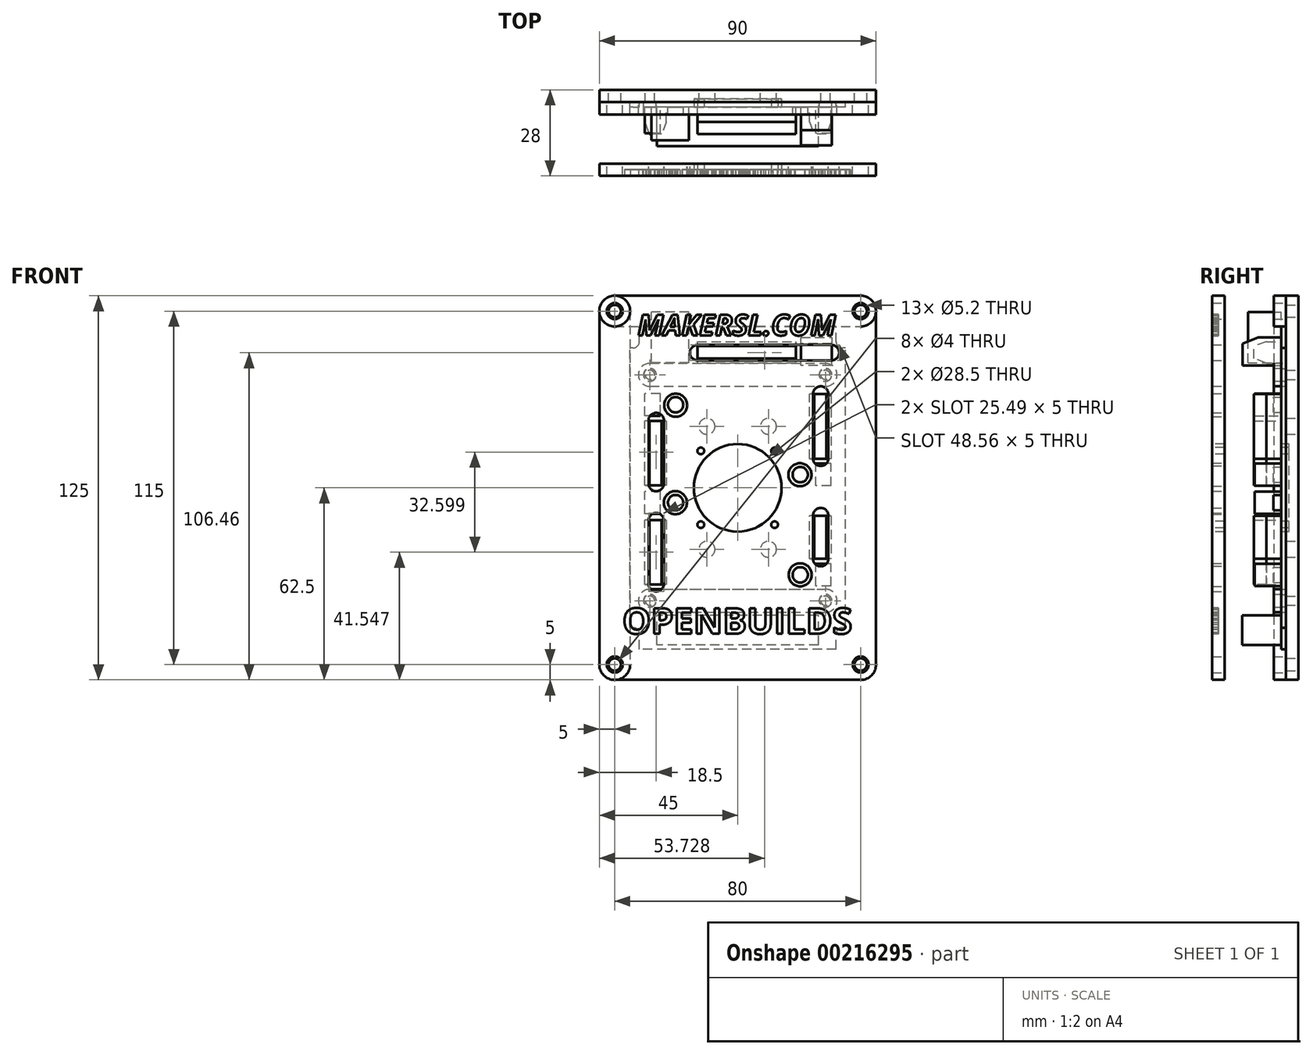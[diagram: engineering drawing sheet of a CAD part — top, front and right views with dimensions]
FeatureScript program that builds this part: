
annotation { "Feature Type Name" : "Feature", "Feature Type Description" : "" }
export const myFeature = defineFeature(function(context is Context, id is Id, definition is map)
    precondition{}
    {
        {
            var Q0;
            Q0=qCreatedBy(makeId("Front.planeOp"),FACE);
            var sketch = newSketch(context, id + "F0", { "sketchPlane" : qUnion([Q0])});
            skPoint(sketch, "E0.middle", {"position": v(0, 0) * mm});
            skLineSegment(sketch, "E1.bottom", {"start": v(10, -20) * mm, "end": v(-10, -20) * mm, "construction": true});
            skLineSegment(sketch, "E1.top", {"start": v(10, 20) * mm, "end": v(-10, 20) * mm, "construction": true});
            skLineSegment(sketch, "E1.left", {"start": v(10, -20) * mm, "end": v(10, 20) * mm, "construction": true});
            skLineSegment(sketch, "E1.right", {"start": v(-10, -20) * mm, "end": v(-10, 20) * mm, "construction": true});
            skCircle(sketch, "E2", {"center": v(-10, 20) * mm, "radius": 2.6 * mm});
            skCircle(sketch, "E3", {"center": v(10, 20) * mm, "radius": 2.6 * mm});
            skCircle(sketch, "E4", {"center": v(10, -20) * mm, "radius": 2.6 * mm});
            skCircle(sketch, "E5", {"center": v(-10, -20) * mm, "radius": 2.6 * mm});
            skLineSegment(sketch, "E6.bottom", {"start": v(28.55, -36.75) * mm, "end": v(-28.55, -36.75) * mm, "construction": true});
            skLineSegment(sketch, "E6.top", {"start": v(28.55, 36.75) * mm, "end": v(-28.55, 36.75) * mm, "construction": true});
            skLineSegment(sketch, "E6.left", {"start": v(28.55, -36.75) * mm, "end": v(28.55, 36.75) * mm, "construction": true});
            skLineSegment(sketch, "E6.right", {"start": v(-28.55, -36.75) * mm, "end": v(-28.55, 36.75) * mm, "construction": true});
            skCircle(sketch, "E7", {"center": v(-28.55, 36.75) * mm, "radius": 1.5 * mm});
            skCircle(sketch, "E8", {"center": v(28.55, 36.75) * mm, "radius": 1.5 * mm});
            skCircle(sketch, "E9", {"center": v(28.55, -36.75) * mm, "radius": 1.5 * mm});
            skCircle(sketch, "E10", {"center": v(-28.55, -36.75) * mm, "radius": 1.5 * mm});
            skLineSegment(sketch, "E11.bottom", {"start": v(40, -62.5) * mm, "end": v(-40, -62.5) * mm});
            skLineSegment(sketch, "E11.top", {"start": v(40, 62.5) * mm, "end": v(-40, 62.5) * mm});
            skLineSegment(sketch, "E11.left", {"start": v(45, -57.5) * mm, "end": v(45, 57.5) * mm});
            skLineSegment(sketch, "E11.right", {"start": v(-45, -57.5) * mm, "end": v(-45, 57.5) * mm});
            skPoint(sketch, "E12.visualSharp", {"position": v(-45, 62.5) * mm});
            skArc(sketch, "E12.filletArc", {"start": v(-40, 62.5) * mm, "mid": v(-43.54, 61.04) * mm, "end": v(-45, 57.5) * mm});
            skPoint(sketch, "E13.visualSharp", {"position": v(45, 62.5) * mm});
            skArc(sketch, "E13.filletArc", {"start": v(45, 57.5) * mm, "mid": v(43.54, 61.04) * mm, "end": v(40, 62.5) * mm});
            skPoint(sketch, "E14.visualSharp", {"position": v(45, -62.5) * mm});
            skArc(sketch, "E14.filletArc", {"start": v(40, -62.5) * mm, "mid": v(43.54, -61.04) * mm, "end": v(45, -57.5) * mm});
            skPoint(sketch, "E15.visualSharp", {"position": v(-45, -62.5) * mm});
            skArc(sketch, "E15.filletArc", {"start": v(-45, -57.5) * mm, "mid": v(-43.54, -61.04) * mm, "end": v(-40, -62.5) * mm});
            skCircle(sketch, "E16", {"center": v(-40, 57.5) * mm, "radius": 2 * mm});
            skCircle(sketch, "E17", {"center": v(40, 57.5) * mm, "radius": 2 * mm});
            skCircle(sketch, "E18", {"center": v(-40, -57.5) * mm, "radius": 2 * mm});
            skCircle(sketch, "E19", {"center": v(40, -57.5) * mm, "radius": 2 * mm});
            skSolve(sketch);
        }
        {
            var Q0;
            Q0=qSketchRegion(id+"F0",true);
            extrude(context, id + "F1", {"entities" : qUnion([Q0]), "depth" : 4 * mm});
        }
        {
            var Q0;
            Q0=makeQuery(id+"F1.opExtrude","CAP_FACE",FACE,{"disambiguationData":[OSD([sQuery(id+"F0.wireOp",EDGE,"E2"),sQuery(id+"F0.wireOp",EDGE,"E3"),sQuery(id+"F0.wireOp",EDGE,"E4"),sQuery(id+"F0.wireOp",EDGE,"E5"),sQuery(id+"F0.wireOp",EDGE,"E7"),sQuery(id+"F0.wireOp",EDGE,"E8"),sQuery(id+"F0.wireOp",EDGE,"E9"),sQuery(id+"F0.wireOp",EDGE,"E10"),sQuery(id+"F0.wireOp",EDGE,"E11.bottom"),sQuery(id+"F0.wireOp",EDGE,"E11.top"),sQuery(id+"F0.wireOp",EDGE,"E11.left"),sQuery(id+"F0.wireOp",EDGE,"E11.right"),sQuery(id+"F0.wireOp",EDGE,"E12.filletArc"),sQuery(id+"F0.wireOp",EDGE,"E13.filletArc"),sQuery(id+"F0.wireOp",EDGE,"E14.filletArc"),sQuery(id+"F0.wireOp",EDGE,"E15.filletArc"),sQuery(id+"F0.wireOp",EDGE,"E16"),sQuery(id+"F0.wireOp",EDGE,"E17"),sQuery(id+"F0.wireOp",EDGE,"E18"),sQuery(id+"F0.wireOp",EDGE,"E19")])],"isStart":false});
            var sketch = newSketch(context, id + "F2", { "sketchPlane" : qUnion([Q0])});
            skCircle(sketch, "E20", {"center": v(-28.55, 36.75) * mm, "radius": 2.1 * mm});
            skCircle(sketch, "E21", {"center": v(28.55, 36.75) * mm, "radius": 2.1 * mm});
            skCircle(sketch, "E22", {"center": v(-28.55, -36.75) * mm, "radius": 2.1 * mm});
            skCircle(sketch, "E23", {"center": v(28.55, -36.75) * mm, "radius": 2.1 * mm});
            skLineSegment(sketch, "E24", {"start": v(-28.55, -36.75) * mm, "end": v(28.55, -36.75) * mm});
            skLineSegment(sketch, "E25", {"start": v(-28.55, 36.75) * mm, "end": v(28.55, 36.75) * mm});
            skArc(sketch, "E26.0.startCap", {"start": v(-28.55, 33) * mm, "mid": v(-32.3, 36.75) * mm, "end": v(-28.55, 40.5) * mm});
            skArc(sketch, "E26.0.endCap", {"start": v(28.55, 40.5) * mm, "mid": v(32.3, 36.75) * mm, "end": v(28.55, 33) * mm});
            skLineSegment(sketch, "E26.0.left", {"start": v(-28.55, 40.5) * mm, "end": v(28.55, 40.5) * mm});
            skLineSegment(sketch, "E26.0.right", {"start": v(-28.55, 33) * mm, "end": v(28.55, 33) * mm});
            skArc(sketch, "E27.0.startCap", {"start": v(-28.55, -40.5) * mm, "mid": v(-32.3, -36.75) * mm, "end": v(-28.55, -33) * mm});
            skArc(sketch, "E27.0.endCap", {"start": v(28.55, -33) * mm, "mid": v(32.3, -36.75) * mm, "end": v(28.55, -40.5) * mm});
            skLineSegment(sketch, "E27.0.left", {"start": v(-28.55, -33) * mm, "end": v(28.55, -33) * mm});
            skLineSegment(sketch, "E27.0.right", {"start": v(-28.55, -40.5) * mm, "end": v(28.55, -40.5) * mm});
            skSolve(sketch);
        }
        {
            var Q0;
            Q0=makeQuery(id+"F2.imprint","IMPRINT",FACE,{"disambiguationData":[TD([[makeQuery(id+"F2.imprint","IMPRINT",EDGE,{"derivedFrom":sQuery(id+"F2.wireOp",EDGE,"E20")}),-1.0]])]});
            var Q1;
            Q1=makeQuery(id+"F2.imprint","IMPRINT",FACE,{"disambiguationData":[TD([[makeQuery(id+"F2.imprint","IMPRINT",EDGE,{"derivedFrom":sQuery(id+"F2.wireOp",EDGE,"E22")}),-1.0]])]});
            extrude(context, id + "F3", {"entities" : qUnion([Q0, Q1]), "depth" : 4 * mm});
        }
        {
            var Q0;
            Q0=makeQuery(id+"F1.opExtrude","CAP_FACE",FACE,{"disambiguationData":[OSD([sQuery(id+"F0.wireOp",EDGE,"E2"),sQuery(id+"F0.wireOp",EDGE,"E3"),sQuery(id+"F0.wireOp",EDGE,"E4"),sQuery(id+"F0.wireOp",EDGE,"E5"),sQuery(id+"F0.wireOp",EDGE,"E7"),sQuery(id+"F0.wireOp",EDGE,"E8"),sQuery(id+"F0.wireOp",EDGE,"E9"),sQuery(id+"F0.wireOp",EDGE,"E10"),sQuery(id+"F0.wireOp",EDGE,"E11.bottom"),sQuery(id+"F0.wireOp",EDGE,"E11.top"),sQuery(id+"F0.wireOp",EDGE,"E11.left"),sQuery(id+"F0.wireOp",EDGE,"E11.right"),sQuery(id+"F0.wireOp",EDGE,"E12.filletArc"),sQuery(id+"F0.wireOp",EDGE,"E13.filletArc"),sQuery(id+"F0.wireOp",EDGE,"E14.filletArc"),sQuery(id+"F0.wireOp",EDGE,"E15.filletArc"),sQuery(id+"F0.wireOp",EDGE,"E16"),sQuery(id+"F0.wireOp",EDGE,"E17"),sQuery(id+"F0.wireOp",EDGE,"E18"),sQuery(id+"F0.wireOp",EDGE,"E19")])],"isStart":false});
            var sketch = newSketch(context, id + "F4", { "sketchPlane" : qUnion([Q0])});
            skCircle(sketch, "E28", {"center": v(-40, 57.5) * mm, "radius": 2.6 * mm});
            skCircle(sketch, "E29", {"center": v(40, 57.5) * mm, "radius": 2.6 * mm});
            skLineSegment(sketch, "E30", {"start": v(-40, 57.5) * mm, "end": v(40, 57.5) * mm});
            skArc(sketch, "E31.0.startCap", {"start": v(-40, 52.5) * mm, "mid": v(-45, 57.5) * mm, "end": v(-40, 62.5) * mm});
            skArc(sketch, "E31.0.endCap", {"start": v(40, 62.5) * mm, "mid": v(45, 57.5) * mm, "end": v(40, 52.5) * mm});
            skLineSegment(sketch, "E31.0.left", {"start": v(-40, 62.5) * mm, "end": v(40, 62.5) * mm});
            skLineSegment(sketch, "E31.0.right", {"start": v(-40, 52.5) * mm, "end": v(40, 52.5) * mm});
            skSolve(sketch);
        }
        {
            var Q0;
            Q0=makeQuery(id+"F4.imprint","IMPRINT",FACE,{"disambiguationData":[TD([[makeQuery(id+"F4.imprint","IMPRINT",EDGE,{"derivedFrom":sQuery(id+"F4.wireOp",EDGE,"E28")}),-1.0]])]});
            extrude(context, id + "F5", {"entities" : qUnion([Q0]), "depth" : 4 * mm});
        }
        {
            var Q0;
            Q0=makeQuery(id+"F1.opExtrude","CAP_FACE",FACE,{"disambiguationData":[OSD([sQuery(id+"F0.wireOp",EDGE,"E2"),sQuery(id+"F0.wireOp",EDGE,"E3"),sQuery(id+"F0.wireOp",EDGE,"E4"),sQuery(id+"F0.wireOp",EDGE,"E5"),sQuery(id+"F0.wireOp",EDGE,"E7"),sQuery(id+"F0.wireOp",EDGE,"E8"),sQuery(id+"F0.wireOp",EDGE,"E9"),sQuery(id+"F0.wireOp",EDGE,"E10"),sQuery(id+"F0.wireOp",EDGE,"E11.bottom"),sQuery(id+"F0.wireOp",EDGE,"E11.top"),sQuery(id+"F0.wireOp",EDGE,"E11.left"),sQuery(id+"F0.wireOp",EDGE,"E11.right"),sQuery(id+"F0.wireOp",EDGE,"E12.filletArc"),sQuery(id+"F0.wireOp",EDGE,"E13.filletArc"),sQuery(id+"F0.wireOp",EDGE,"E14.filletArc"),sQuery(id+"F0.wireOp",EDGE,"E15.filletArc"),sQuery(id+"F0.wireOp",EDGE,"E16"),sQuery(id+"F0.wireOp",EDGE,"E17"),sQuery(id+"F0.wireOp",EDGE,"E18"),sQuery(id+"F0.wireOp",EDGE,"E19")])],"isStart":false});
            var sketch = newSketch(context, id + "F6", { "sketchPlane" : qUnion([Q0])});
            skCircle(sketch, "E32", {"center": v(-40, -57.5) * mm, "radius": 2.6 * mm});
            skCircle(sketch, "E33", {"center": v(-40, 57.5) * mm, "radius": 2.6 * mm});
            skLineSegment(sketch, "E34", {"start": v(-40, 57.5) * mm, "end": v(-40, -57.5) * mm});
            skArc(sketch, "E35.0.startCap", {"start": v(-45, 57.5) * mm, "mid": v(-40, 62.5) * mm, "end": v(-35, 57.5) * mm});
            skArc(sketch, "E35.0.endCap", {"start": v(-35, -57.5) * mm, "mid": v(-40, -62.5) * mm, "end": v(-45, -57.5) * mm});
            skLineSegment(sketch, "E35.0.left", {"start": v(-35, 57.5) * mm, "end": v(-35, -57.5) * mm});
            skLineSegment(sketch, "E35.0.right", {"start": v(-45, 57.5) * mm, "end": v(-45, -57.5) * mm});
            skSolve(sketch);
        }
        {
            var Q0;
            Q0=makeQuery(id+"F6.imprint","IMPRINT",FACE,{"disambiguationData":[TD([[makeQuery(id+"F6.imprint","IMPRINT",EDGE,{"derivedFrom":sQuery(id+"F6.wireOp",EDGE,"E32")}),-1.0]])]});
            extrude(context, id + "F7", {"entities" : qUnion([Q0]), "depth" : 4 * mm});
        }
        {
            var Q0;
            Q0=makeQuery(id+"F1.opExtrude","CAP_FACE",FACE,{"disambiguationData":[OSD([sQuery(id+"F0.wireOp",EDGE,"E2"),sQuery(id+"F0.wireOp",EDGE,"E3"),sQuery(id+"F0.wireOp",EDGE,"E4"),sQuery(id+"F0.wireOp",EDGE,"E5"),sQuery(id+"F0.wireOp",EDGE,"E7"),sQuery(id+"F0.wireOp",EDGE,"E8"),sQuery(id+"F0.wireOp",EDGE,"E9"),sQuery(id+"F0.wireOp",EDGE,"E10"),sQuery(id+"F0.wireOp",EDGE,"E11.bottom"),sQuery(id+"F0.wireOp",EDGE,"E11.top"),sQuery(id+"F0.wireOp",EDGE,"E11.left"),sQuery(id+"F0.wireOp",EDGE,"E11.right"),sQuery(id+"F0.wireOp",EDGE,"E12.filletArc"),sQuery(id+"F0.wireOp",EDGE,"E13.filletArc"),sQuery(id+"F0.wireOp",EDGE,"E14.filletArc"),sQuery(id+"F0.wireOp",EDGE,"E15.filletArc"),sQuery(id+"F0.wireOp",EDGE,"E16"),sQuery(id+"F0.wireOp",EDGE,"E17"),sQuery(id+"F0.wireOp",EDGE,"E18"),sQuery(id+"F0.wireOp",EDGE,"E19")])],"isStart":false});
            var sketch = newSketch(context, id + "F8", { "sketchPlane" : qUnion([Q0])});
            skLineSegment(sketch, "E36.bottom", {"start": v(32, -52.5) * mm, "end": v(-32, -52.5) * mm});
            skLineSegment(sketch, "E36.top", {"start": v(32, 52.5) * mm, "end": v(-32, 52.5) * mm});
            skLineSegment(sketch, "E36.left", {"start": v(35, -45.5) * mm, "end": v(35, 45.5) * mm});
            skLineSegment(sketch, "E36.right", {"start": v(-35, -45.5) * mm, "end": v(-35, 45.5) * mm});
            skPoint(sketch, "E36.middle", {"position": v(0, 0) * mm});
            skLineSegment(sketch, "E37.bottom", {"start": v(-34, 45.5) * mm, "end": v(-35, 45.5) * mm});
            skLineSegment(sketch, "E37.left", {"start": v(-32, 47.5) * mm, "end": v(-32, 52.5) * mm});
            skPoint(sketch, "E37.middle", {"position": v(-35, 52.5) * mm});
            skLineSegment(sketch, "E38.bottom", {"start": v(35, 45.5) * mm, "end": v(34, 45.5) * mm});
            skLineSegment(sketch, "E38.right", {"start": v(32, 47.5) * mm, "end": v(32, 52.5) * mm});
            skPoint(sketch, "E38.middle", {"position": v(35, 52.5) * mm});
            skLineSegment(sketch, "E39.top", {"start": v(35, -45.5) * mm, "end": v(34, -45.5) * mm});
            skLineSegment(sketch, "E39.right", {"start": v(32, -52.5) * mm, "end": v(32, -47.5) * mm});
            skPoint(sketch, "E39.middle", {"position": v(35, -52.5) * mm});
            skLineSegment(sketch, "E40.top", {"start": v(-35, -45.5) * mm, "end": v(-34, -45.5) * mm});
            skLineSegment(sketch, "E40.right", {"start": v(-32, -52.5) * mm, "end": v(-32, -47.5) * mm});
            skPoint(sketch, "E40.middle", {"position": v(-35, -52.5) * mm});
            skPoint(sketch, "E40.left.end.orphan", {"position": v(-38, -45.5) * mm});
            skPoint(sketch, "E40.bottom.start.orphan", {"position": v(-38, -59.5) * mm});
            skPoint(sketch, "E41.orphan", {"position": v(-32, -59.5) * mm});
            skPoint(sketch, "E42.visualSharp", {"position": v(-32, -45.5) * mm});
            skArc(sketch, "E42.filletArc", {"start": v(-32, -47.5) * mm, "mid": v(-32.59, -46.09) * mm, "end": v(-34, -45.5) * mm});
            skPoint(sketch, "E43.visualSharp", {"position": v(32, -45.5) * mm});
            skArc(sketch, "E43.filletArc", {"start": v(34, -45.5) * mm, "mid": v(32.59, -46.09) * mm, "end": v(32, -47.5) * mm});
            skPoint(sketch, "E44.visualSharp", {"position": v(32, 45.5) * mm});
            skArc(sketch, "E44.filletArc", {"start": v(32, 47.5) * mm, "mid": v(32.59, 46.09) * mm, "end": v(34, 45.5) * mm});
            skPoint(sketch, "E45.visualSharp", {"position": v(-32, 45.5) * mm});
            skArc(sketch, "E45.filletArc", {"start": v(-34, 45.5) * mm, "mid": v(-32.59, 46.09) * mm, "end": v(-32, 47.5) * mm});
            skPoint(sketch, "E37.right.end.orphan", {"position": v(-38, 59.5) * mm});
            skPoint(sketch, "E46.orphan", {"position": v(-38, 45.5) * mm});
            skPoint(sketch, "E47.orphan", {"position": v(-32, 59.5) * mm});
            skPoint(sketch, "E38.left.start.orphan", {"position": v(38, 45.5) * mm});
            skPoint(sketch, "E38.top.end.orphan", {"position": v(32, 59.5) * mm});
            skPoint(sketch, "E38.top.start.orphan", {"position": v(38, 59.5) * mm});
            skPoint(sketch, "E39.bottom.end.orphan", {"position": v(32, -59.5) * mm});
            skPoint(sketch, "E39.left.end.orphan", {"position": v(38, -45.5) * mm});
            skPoint(sketch, "E39.left.start.orphan", {"position": v(38, -59.5) * mm});
            skCircle(sketch, "E48", {"center": v(-28.55, 36.75) * mm, "radius": 2 * mm});
            skCircle(sketch, "E49", {"center": v(28.55, 36.75) * mm, "radius": 2 * mm});
            skCircle(sketch, "E50", {"center": v(28.55, -36.75) * mm, "radius": 2 * mm});
            skCircle(sketch, "E51", {"center": v(-28.55, -36.75) * mm, "radius": 2 * mm});
            skSolve(sketch);
        }
        {
            var Q0;
            Q0=qSketchRegion(id+"F8",true);
            extrude(context, id + "F9", {"entities" : qUnion([Q0]), "depth" : 1.6 * mm});
        }
        {
            var Q0;
            Q0=makeQuery(id+"F9.opExtrude","CAP_FACE",FACE,{"disambiguationData":[OSD([sQuery(id+"F8.wireOp",EDGE,"E36.bottom"),sQuery(id+"F8.wireOp",EDGE,"E36.top"),sQuery(id+"F8.wireOp",EDGE,"E36.left"),sQuery(id+"F8.wireOp",EDGE,"E36.right"),sQuery(id+"F8.wireOp",EDGE,"E37.bottom"),sQuery(id+"F8.wireOp",EDGE,"E37.left"),sQuery(id+"F8.wireOp",EDGE,"E38.bottom"),sQuery(id+"F8.wireOp",EDGE,"E38.right"),sQuery(id+"F8.wireOp",EDGE,"E39.top"),sQuery(id+"F8.wireOp",EDGE,"E39.right"),sQuery(id+"F8.wireOp",EDGE,"E40.top"),sQuery(id+"F8.wireOp",EDGE,"E40.right"),sQuery(id+"F8.wireOp",EDGE,"E42.filletArc"),sQuery(id+"F8.wireOp",EDGE,"E43.filletArc"),sQuery(id+"F8.wireOp",EDGE,"E44.filletArc"),sQuery(id+"F8.wireOp",EDGE,"E45.filletArc"),sQuery(id+"F8.wireOp",EDGE,"E48"),sQuery(id+"F8.wireOp",EDGE,"E49"),sQuery(id+"F8.wireOp",EDGE,"E50"),sQuery(id+"F8.wireOp",EDGE,"E51")])],"isStart":false});
            var sketch = newSketch(context, id + "F10", { "sketchPlane" : qUnion([Q0])});
            skLineSegment(sketch, "E52.bottom", {"start": v(-15.9, 40.7) * mm, "end": v(-28.1, 40.7) * mm});
            skLineSegment(sketch, "E52.top", {"start": v(-15.9, 57.2) * mm, "end": v(-28.1, 57.2) * mm});
            skLineSegment(sketch, "E52.left", {"start": v(-15.9, 40.7) * mm, "end": v(-15.9, 57.2) * mm});
            skLineSegment(sketch, "E52.right", {"start": v(-28.1, 40.7) * mm, "end": v(-28.1, 57.2) * mm});
            skPoint(sketch, "E52.middle", {"position": v(-22, 48.95) * mm});
            skLineSegment(sketch, "E53.bottom", {"start": v(30.6, 39.8) * mm, "end": v(20.6, 39.8) * mm});
            skLineSegment(sketch, "E53.top", {"start": v(30.6, 48.9) * mm, "end": v(20.6, 48.9) * mm});
            skLineSegment(sketch, "E53.left", {"start": v(30.6, 39.8) * mm, "end": v(30.6, 48.9) * mm});
            skLineSegment(sketch, "E53.right", {"start": v(20.6, 39.8) * mm, "end": v(20.6, 48.9) * mm});
            skPoint(sketch, "E53.middle", {"position": v(25.6, 44.35) * mm});
            skLineSegment(sketch, "E54.bottom", {"start": v(18.9, 40.6) * mm, "end": v(-13.1, 40.6) * mm});
            skLineSegment(sketch, "E54.top", {"start": v(18.9, 47.6) * mm, "end": v(-13.1, 47.6) * mm});
            skLineSegment(sketch, "E54.left", {"start": v(18.9, 40.6) * mm, "end": v(18.9, 47.6) * mm});
            skLineSegment(sketch, "E54.right", {"start": v(-13.1, 40.6) * mm, "end": v(-13.1, 47.6) * mm});
            skPoint(sketch, "E54.middle", {"position": v(2.9, 44.1) * mm});
            skLineSegment(sketch, "E55.bottom", {"start": v(30.35, 9.5) * mm, "end": v(23.35, 9.5) * mm});
            skLineSegment(sketch, "E55.top", {"start": v(30.35, 30.5) * mm, "end": v(23.35, 30.5) * mm});
            skLineSegment(sketch, "E55.left", {"start": v(30.35, 9.5) * mm, "end": v(30.35, 30.5) * mm});
            skLineSegment(sketch, "E55.right", {"start": v(23.35, 9.5) * mm, "end": v(23.35, 30.5) * mm});
            skPoint(sketch, "E55.middle", {"position": v(26.85, 20) * mm});
            skLineSegment(sketch, "E56.bottom", {"start": v(-23.2, -31.5) * mm, "end": v(-30.2, -31.5) * mm});
            skLineSegment(sketch, "E56.top", {"start": v(-23.2, -10.5) * mm, "end": v(-30.2, -10.5) * mm});
            skLineSegment(sketch, "E56.left", {"start": v(-23.2, -31.5) * mm, "end": v(-23.2, -10.5) * mm});
            skLineSegment(sketch, "E56.right", {"start": v(-30.2, -31.5) * mm, "end": v(-30.2, -10.5) * mm});
            skPoint(sketch, "E56.middle", {"position": v(-26.7, -21) * mm});
            skLineSegment(sketch, "E57.bottom", {"start": v(-23.2, 0.8) * mm, "end": v(-30.2, 0.8) * mm});
            skLineSegment(sketch, "E57.top", {"start": v(-23.2, 21.8) * mm, "end": v(-30.2, 21.8) * mm});
            skLineSegment(sketch, "E57.left", {"start": v(-23.2, 0.8) * mm, "end": v(-23.2, 21.8) * mm});
            skLineSegment(sketch, "E57.right", {"start": v(-30.2, 0.8) * mm, "end": v(-30.2, 21.8) * mm});
            skPoint(sketch, "E57.middle", {"position": v(-26.7, 11.3) * mm});
            skLineSegment(sketch, "E58.bottom", {"start": v(26.25, -51.1) * mm, "end": v(-26.25, -51.1) * mm});
            skLineSegment(sketch, "E58.top", {"start": v(26.25, -41.5) * mm, "end": v(-26.25, -41.5) * mm});
            skLineSegment(sketch, "E58.left", {"start": v(26.25, -51.1) * mm, "end": v(26.25, -41.5) * mm});
            skLineSegment(sketch, "E58.right", {"start": v(-26.25, -51.1) * mm, "end": v(-26.25, -41.5) * mm});
            skPoint(sketch, "E58.middle", {"position": v(0, -46.3) * mm});
            skLineSegment(sketch, "E59.bottom", {"start": v(30.35, -23.1) * mm, "end": v(23.35, -23.1) * mm});
            skLineSegment(sketch, "E59.top", {"start": v(30.35, -9.1) * mm, "end": v(23.35, -9.1) * mm});
            skLineSegment(sketch, "E59.left", {"start": v(30.35, -23.1) * mm, "end": v(30.35, -9.1) * mm});
            skLineSegment(sketch, "E59.right", {"start": v(23.35, -23.1) * mm, "end": v(23.35, -9.1) * mm});
            skPoint(sketch, "E59.middle", {"position": v(26.85, -16.1) * mm});
            skLineSegment(sketch, "E60.bottom", {"start": v(30.35, -31.95) * mm, "end": v(25.35, -31.95) * mm});
            skLineSegment(sketch, "E60.top", {"start": v(30.35, -24.7) * mm, "end": v(25.35, -24.7) * mm});
            skLineSegment(sketch, "E60.left", {"start": v(30.35, -31.95) * mm, "end": v(30.35, -24.7) * mm});
            skLineSegment(sketch, "E60.right", {"start": v(25.35, -31.95) * mm, "end": v(25.35, -24.7) * mm});
            skPoint(sketch, "E60.middle", {"position": v(27.85, -28.33) * mm});
            skLineSegment(sketch, "E61.bottom", {"start": v(30.35, 0.65) * mm, "end": v(25.35, 0.65) * mm});
            skLineSegment(sketch, "E61.top", {"start": v(30.35, 7.9) * mm, "end": v(25.35, 7.9) * mm});
            skLineSegment(sketch, "E61.left", {"start": v(30.35, 0.65) * mm, "end": v(30.35, 7.9) * mm});
            skLineSegment(sketch, "E61.right", {"start": v(25.35, 0.65) * mm, "end": v(25.35, 7.9) * mm});
            skPoint(sketch, "E61.middle", {"position": v(27.85, 4.28) * mm});
            skLineSegment(sketch, "E62.bottom", {"start": v(-25.2, 23.4) * mm, "end": v(-30.2, 23.4) * mm});
            skLineSegment(sketch, "E62.top", {"start": v(-25.2, 30.65) * mm, "end": v(-30.2, 30.65) * mm});
            skLineSegment(sketch, "E62.left", {"start": v(-25.2, 23.4) * mm, "end": v(-25.2, 30.65) * mm});
            skLineSegment(sketch, "E62.right", {"start": v(-30.2, 23.4) * mm, "end": v(-30.2, 30.65) * mm});
            skPoint(sketch, "E62.middle", {"position": v(-27.7, 27.02) * mm});
            skLineSegment(sketch, "E63.bottom", {"start": v(-25.2, -8.45) * mm, "end": v(-30.2, -8.45) * mm});
            skLineSegment(sketch, "E63.top", {"start": v(-25.2, -1.2) * mm, "end": v(-30.2, -1.2) * mm});
            skLineSegment(sketch, "E63.left", {"start": v(-25.2, -8.45) * mm, "end": v(-25.2, -1.2) * mm});
            skLineSegment(sketch, "E63.right", {"start": v(-30.2, -8.45) * mm, "end": v(-30.2, -1.2) * mm});
            skPoint(sketch, "E63.middle", {"position": v(-27.7, -4.83) * mm});
            skCircle(sketch, "E64", {"center": v(-20.2, 27.02) * mm, "radius": 2.5 * mm});
            skCircle(sketch, "E65", {"center": v(20.35, 4.28) * mm, "radius": 2.5 * mm});
            skCircle(sketch, "E66", {"center": v(20.35, -28.33) * mm, "radius": 2.5 * mm});
            skCircle(sketch, "E67", {"center": v(-20.2, -4.83) * mm, "radius": 2.5 * mm});
            skPoint(sketch, "E67.centerSnap0", {"position": v(-25.2, -4.83) * mm});
            skSolve(sketch);
        }
        {
            var Q0;
            {var subQ0=sQuery(id+"F10.wireOp",EDGE,"E52.top");Q0=makeQuery(id+"F10.imprint","IMPRINT",FACE,{"disambiguationData":[TD([[makeQuery(id+"F10.imprint","IMPRINT",EDGE,{"derivedFrom":subQ0}),1.0]])]});}
            var Q1;
            {var subQ0=sQuery(id+"F10.wireOp",EDGE,"E52.bottom");Q1=makeQuery(id+"F10.imprint","IMPRINT",FACE,{"disambiguationData":[TD([[makeQuery(id+"F10.imprint","IMPRINT",EDGE,{"derivedFrom":subQ0}),-1.0]])]});}
            extrude(context, id + "F11", {"entities" : qUnion([Q0, Q1]), "depth" : 10.8 * mm});
        }
        {
            var Q0;
            Q0=makeQuery(id+"F10.imprint","IMPRINT",FACE,{"disambiguationData":[TD([[makeQuery(id+"F10.imprint","IMPRINT",EDGE,{"derivedFrom":sQuery(id+"F10.wireOp",EDGE,"E53.bottom")}),-1.0]])]});
            extrude(context, id + "F12", {"entities" : qUnion([Q0]), "depth" : 12.5 * mm});
        }
        {
            var Q0;
            Q0=makeQuery(id+"F10.imprint","IMPRINT",FACE,{"disambiguationData":[TD([[makeQuery(id+"F10.imprint","IMPRINT",EDGE,{"derivedFrom":sQuery(id+"F10.wireOp",EDGE,"E54.bottom")}),-1.0]])]});
            extrude(context, id + "F13", {"entities" : qUnion([Q0]), "depth" : 8.85 * mm});
        }
        {
            var Q0;
            Q0=makeQuery(id+"F13.opExtrude","CAP_EDGE",EDGE,{"disambiguationData":[OSD([sQuery(id+"F10.wireOp",EDGE,"E54.top")])],"isStart":false});
            var Q1;
            Q1=makeQuery(id+"F13.opExtrude","CAP_EDGE",EDGE,{"disambiguationData":[OSD([sQuery(id+"F10.wireOp",EDGE,"E54.bottom")])],"isStart":false});
            chamfer(context, id + "F14", {"entities" : qUnion([Q0, Q1]), "chamferType" : ChamferType.TWO_OFFSETS, "width1" : 1.5 * mm, "oppositeDirection" : false, "width2" : 4 * mm, "tangentPropagation" : true});
        }
        {
            var Q0;
            Q0=makeQuery(id+"F12.opExtrude","CAP_EDGE",EDGE,{"disambiguationData":[OSD([sQuery(id+"F10.wireOp",EDGE,"E53.top")])],"isStart":false});
            chamfer(context, id + "F15", {"entities" : qUnion([Q0]), "chamferType" : ChamferType.TWO_OFFSETS, "width1" : 2 * mm, "oppositeDirection" : false, "width2" : 5 * mm, "tangentPropagation" : true});
        }
        {
            var Q0;
            Q0=makeQuery(id+"F10.imprint","IMPRINT",FACE,{"disambiguationData":[TD([[makeQuery(id+"F10.imprint","IMPRINT",EDGE,{"derivedFrom":sQuery(id+"F10.wireOp",EDGE,"E55.bottom")}),-1.0]])]});
            var Q1;
            Q1=makeQuery(id+"F10.imprint","IMPRINT",FACE,{"disambiguationData":[TD([[makeQuery(id+"F10.imprint","IMPRINT",EDGE,{"derivedFrom":sQuery(id+"F10.wireOp",EDGE,"E57.bottom")}),-1.0]])]});
            var Q2;
            Q2=makeQuery(id+"F10.imprint","IMPRINT",FACE,{"disambiguationData":[TD([[makeQuery(id+"F10.imprint","IMPRINT",EDGE,{"derivedFrom":sQuery(id+"F10.wireOp",EDGE,"E56.bottom")}),-1.0]])]});
            extrude(context, id + "F16", {"entities" : qUnion([Q0, Q1, Q2]), "depth" : 8.8 * mm});
        }
        {
            var Q0;
            Q0=makeQuery(id+"F10.imprint","IMPRINT",FACE,{"disambiguationData":[TD([[makeQuery(id+"F10.imprint","IMPRINT",EDGE,{"derivedFrom":sQuery(id+"F10.wireOp",EDGE,"E58.bottom")}),-1.0]])]});
            extrude(context, id + "F17", {"entities" : qUnion([Q0]), "depth" : 12.7 * mm});
        }
        {
            var Q0;
            Q0=makeQuery(id+"F10.imprint","IMPRINT",FACE,{"disambiguationData":[TD([[makeQuery(id+"F10.imprint","IMPRINT",EDGE,{"derivedFrom":sQuery(id+"F10.wireOp",EDGE,"E59.bottom")}),-1.0]])]});
            extrude(context, id + "F18", {"entities" : qUnion([Q0]), "depth" : 8.8 * mm});
        }
        {
            var Q0;
            Q0=makeQuery(id+"F18.opExtrude","CAP_EDGE",EDGE,{"disambiguationData":[OSD([sQuery(id+"F10.wireOp",EDGE,"E59.left")])],"isStart":false});
            var Q1;
            Q1=makeQuery(id+"F18.opExtrude","CAP_EDGE",EDGE,{"disambiguationData":[OSD([sQuery(id+"F10.wireOp",EDGE,"E59.right")])],"isStart":false});
            chamfer(context, id + "F19", {"entities" : qUnion([Q0, Q1]), "chamferType" : ChamferType.TWO_OFFSETS, "width1" : 1.5 * mm, "oppositeDirection" : false, "width2" : 4 * mm, "tangentPropagation" : true});
        }
        {
            var Q0;
            Q0=makeQuery(id+"F10.imprint","IMPRINT",FACE,{"disambiguationData":[TD([[makeQuery(id+"F10.imprint","IMPRINT",EDGE,{"derivedFrom":sQuery(id+"F10.wireOp",EDGE,"E62.bottom")}),-1.0]])]});
            var Q1;
            Q1=makeQuery(id+"F10.imprint","IMPRINT",FACE,{"disambiguationData":[TD([[makeQuery(id+"F10.imprint","IMPRINT",EDGE,{"derivedFrom":sQuery(id+"F10.wireOp",EDGE,"E63.bottom")}),-1.0]])]});
            var Q2;
            Q2=makeQuery(id+"F10.imprint","IMPRINT",FACE,{"disambiguationData":[TD([[makeQuery(id+"F10.imprint","IMPRINT",EDGE,{"derivedFrom":sQuery(id+"F10.wireOp",EDGE,"E61.bottom")}),-1.0]])]});
            var Q3;
            Q3=makeQuery(id+"F10.imprint","IMPRINT",FACE,{"disambiguationData":[TD([[makeQuery(id+"F10.imprint","IMPRINT",EDGE,{"derivedFrom":sQuery(id+"F10.wireOp",EDGE,"E60.bottom")}),-1.0]])]});
            extrude(context, id + "F20", {"entities" : qUnion([Q0, Q1, Q2, Q3]), "depth" : 8.6 * mm});
        }
        {
            var Q0;
            Q0=makeQuery(id+"F16.opExtrude","CAP_EDGE",EDGE,{"disambiguationData":[OSD([sQuery(id+"F10.wireOp",EDGE,"E57.right")])],"isStart":false});
            var Q1;
            Q1=makeQuery(id+"F16.opExtrude","CAP_EDGE",EDGE,{"disambiguationData":[OSD([sQuery(id+"F10.wireOp",EDGE,"E57.left")])],"isStart":false});
            var Q2;
            Q2=makeQuery(id+"F16.opExtrude","CAP_EDGE",EDGE,{"disambiguationData":[OSD([sQuery(id+"F10.wireOp",EDGE,"E55.right")])],"isStart":false});
            var Q3;
            Q3=makeQuery(id+"F16.opExtrude","CAP_EDGE",EDGE,{"disambiguationData":[OSD([sQuery(id+"F10.wireOp",EDGE,"E55.left")])],"isStart":false});
            var Q4;
            Q4=makeQuery(id+"F16.opExtrude","CAP_EDGE",EDGE,{"disambiguationData":[OSD([sQuery(id+"F10.wireOp",EDGE,"E56.right")])],"isStart":false});
            var Q5;
            Q5=makeQuery(id+"F16.opExtrude","CAP_EDGE",EDGE,{"disambiguationData":[OSD([sQuery(id+"F10.wireOp",EDGE,"E56.left")])],"isStart":false});
            chamfer(context, id + "F21", {"entities" : qUnion([Q0, Q1, Q2, Q3, Q4, Q5]), "chamferType" : ChamferType.TWO_OFFSETS, "width1" : 4 * mm, "oppositeDirection" : false, "width2" : 1.5 * mm, "tangentPropagation" : true});
        }
        {
            var Q0;
            Q0=makeQuery(id+"F10.imprint","IMPRINT",FACE,{"disambiguationData":[TD([[makeQuery(id+"F10.imprint","IMPRINT",EDGE,{"derivedFrom":sQuery(id+"F10.wireOp",EDGE,"E64")}),1.0]])]});
            var Q1;
            Q1=makeQuery(id+"F10.imprint","IMPRINT",FACE,{"disambiguationData":[TD([[makeQuery(id+"F10.imprint","IMPRINT",EDGE,{"derivedFrom":sQuery(id+"F10.wireOp",EDGE,"E65")}),1.0]])]});
            var Q2;
            Q2=makeQuery(id+"F10.imprint","IMPRINT",FACE,{"disambiguationData":[TD([[makeQuery(id+"F10.imprint","IMPRINT",EDGE,{"derivedFrom":sQuery(id+"F10.wireOp",EDGE,"E67")}),1.0]])]});
            var Q3;
            Q3=makeQuery(id+"F10.imprint","IMPRINT",FACE,{"disambiguationData":[TD([[makeQuery(id+"F10.imprint","IMPRINT",EDGE,{"derivedFrom":sQuery(id+"F10.wireOp",EDGE,"E66")}),1.0]])]});
            extrude(context, id + "F22", {"entities" : qUnion([Q0, Q1, Q2, Q3]), "depth" : 2.5 * mm});
        }
        {
            var Q0;
            Q0=makeQuery(id+"F1.opExtrude","CAP_FACE",FACE,{"disambiguationData":[OSD([sQuery(id+"F0.wireOp",EDGE,"E2"),sQuery(id+"F0.wireOp",EDGE,"E3"),sQuery(id+"F0.wireOp",EDGE,"E4"),sQuery(id+"F0.wireOp",EDGE,"E5"),sQuery(id+"F0.wireOp",EDGE,"E7"),sQuery(id+"F0.wireOp",EDGE,"E8"),sQuery(id+"F0.wireOp",EDGE,"E9"),sQuery(id+"F0.wireOp",EDGE,"E10"),sQuery(id+"F0.wireOp",EDGE,"E11.bottom"),sQuery(id+"F0.wireOp",EDGE,"E11.top"),sQuery(id+"F0.wireOp",EDGE,"E11.left"),sQuery(id+"F0.wireOp",EDGE,"E11.right"),sQuery(id+"F0.wireOp",EDGE,"E12.filletArc"),sQuery(id+"F0.wireOp",EDGE,"E13.filletArc"),sQuery(id+"F0.wireOp",EDGE,"E14.filletArc"),sQuery(id+"F0.wireOp",EDGE,"E15.filletArc"),sQuery(id+"F0.wireOp",EDGE,"E16"),sQuery(id+"F0.wireOp",EDGE,"E17"),sQuery(id+"F0.wireOp",EDGE,"E18"),sQuery(id+"F0.wireOp",EDGE,"E19")])],"isStart":false});
            var sketch = newSketch(context, id + "F23", { "sketchPlane" : qUnion([Q0])});
            skCircle(sketch, "E68", {"center": v(-40, 57.5) * mm, "radius": 2.6 * mm});
            skCircle(sketch, "E69", {"center": v(-40, 57.5) * mm, "radius": 5 * mm});
            skSolve(sketch);
        }
        {
            var Q0;
            Q0=makeQuery(id+"F23.imprint","IMPRINT",FACE,{"disambiguationData":[TD([[makeQuery(id+"F23.imprint","IMPRINT",EDGE,{"derivedFrom":sQuery(id+"F23.wireOp",EDGE,"E68")}),-1.0]])]});
            extrude(context, id + "F24", {"entities" : qUnion([Q0]), "depth" : 4 * mm});
        }
        {
            var Q0;
            Q0=makeQuery(id+"F1.opExtrude","CAP_FACE",FACE,{"disambiguationData":[OSD([sQuery(id+"F0.wireOp",EDGE,"E2"),sQuery(id+"F0.wireOp",EDGE,"E3"),sQuery(id+"F0.wireOp",EDGE,"E4"),sQuery(id+"F0.wireOp",EDGE,"E5"),sQuery(id+"F0.wireOp",EDGE,"E7"),sQuery(id+"F0.wireOp",EDGE,"E8"),sQuery(id+"F0.wireOp",EDGE,"E9"),sQuery(id+"F0.wireOp",EDGE,"E10"),sQuery(id+"F0.wireOp",EDGE,"E11.bottom"),sQuery(id+"F0.wireOp",EDGE,"E11.top"),sQuery(id+"F0.wireOp",EDGE,"E11.left"),sQuery(id+"F0.wireOp",EDGE,"E11.right"),sQuery(id+"F0.wireOp",EDGE,"E12.filletArc"),sQuery(id+"F0.wireOp",EDGE,"E13.filletArc"),sQuery(id+"F0.wireOp",EDGE,"E14.filletArc"),sQuery(id+"F0.wireOp",EDGE,"E15.filletArc"),sQuery(id+"F0.wireOp",EDGE,"E16"),sQuery(id+"F0.wireOp",EDGE,"E17"),sQuery(id+"F0.wireOp",EDGE,"E18"),sQuery(id+"F0.wireOp",EDGE,"E19")])],"isStart":false});
            cPlane(context, id + "F25", {"entities" : qUnion([Q0]), "cplaneType" : CPlaneType.OFFSET, "offset" : 20 * mm, "width" : 150 * mm, "height" : 150 * mm});
        }
        {
            var Q0;
            Q0=qCreatedBy(id+"F25.planeOp",FACE);
            var sketch = newSketch(context, id + "F26", { "sketchPlane" : qUnion([Q0])});
            skLineSegment(sketch, "E70.bottom", {"start": v(40, -57.5) * mm, "end": v(-40, -57.5) * mm, "construction": true});
            skLineSegment(sketch, "E70.top", {"start": v(40, 57.5) * mm, "end": v(-40, 57.5) * mm, "construction": true});
            skLineSegment(sketch, "E70.left", {"start": v(40, -57.5) * mm, "end": v(40, 57.5) * mm, "construction": true});
            skLineSegment(sketch, "E70.right", {"start": v(-40, -57.5) * mm, "end": v(-40, 57.5) * mm, "construction": true});
            skPoint(sketch, "E70.middle", {"position": v(0, 0) * mm});
            skCircle(sketch, "E71", {"center": v(-40, 57.5) * mm, "radius": 2.6 * mm});
            skCircle(sketch, "E72.0.1.0", {"center": v(-40, -57.5) * mm, "radius": 2.6 * mm});
            skLineSegment(sketch, "E72.direction1", {"start": v(-40, 57.5) * mm, "end": v(40, 57.5) * mm, "construction": true});
            skLineSegment(sketch, "E72.direction2", {"start": v(-40, 57.5) * mm, "end": v(-40, -57.5) * mm, "construction": true});
            skLineSegment(sketch, "E73.bottom", {"start": v(40, -62.5) * mm, "end": v(-40, -62.5) * mm});
            skLineSegment(sketch, "E73.top", {"start": v(40, 62.5) * mm, "end": v(-40, 62.5) * mm});
            skLineSegment(sketch, "E73.left", {"start": v(45, -57.5) * mm, "end": v(45, 57.5) * mm});
            skLineSegment(sketch, "E73.right", {"start": v(-45, -57.5) * mm, "end": v(-45, 57.5) * mm});
            skLineSegment(sketch, "E74", {"start": v(-13.05, 43.96) * mm, "end": v(30.5, 43.96) * mm});
            skLineSegment(sketch, "E75", {"start": v(-26.5, 21.9) * mm, "end": v(-26.5, 1.4) * mm});
            skLineSegment(sketch, "E76", {"start": v(27, 30.52) * mm, "end": v(27, 9.6) * mm});
            skLineSegment(sketch, "E77", {"start": v(-26.5, -10.7) * mm, "end": v(-26.5, -31.2) * mm});
            skLineSegment(sketch, "E78", {"start": v(27, -9.05) * mm, "end": v(27, -23.05) * mm});
            skArc(sketch, "E79.0.startCap", {"start": v(-13.05, 41.46) * mm, "mid": v(-15.55, 43.96) * mm, "end": v(-13.05, 46.46) * mm});
            skArc(sketch, "E79.0.endCap", {"start": v(30.5, 46.46) * mm, "mid": v(33, 43.96) * mm, "end": v(30.5, 41.46) * mm});
            skLineSegment(sketch, "E79.0.left", {"start": v(-13.05, 46.46) * mm, "end": v(30.5, 46.46) * mm});
            skLineSegment(sketch, "E79.0.right", {"start": v(-13.05, 41.46) * mm, "end": v(30.5, 41.46) * mm});
            skCircle(sketch, "E80", {"center": v(-20.18, 26.88) * mm, "radius": 3.75 * mm});
            skCircle(sketch, "E81", {"center": v(20.25, 4.25) * mm, "radius": 3.75 * mm});
            skCircle(sketch, "E82", {"center": v(-20.27, -4.83) * mm, "radius": 3.75 * mm});
            skCircle(sketch, "E83", {"center": v(20.32, -28.31) * mm, "radius": 3.75 * mm});
            skCircle(sketch, "E84.0.1.0", {"center": v(40, 57.5) * mm, "radius": 2.6 * mm});
            skCircle(sketch, "E84.0.1.1", {"center": v(40, -57.5) * mm, "radius": 2.6 * mm});
            skPoint(sketch, "E85.visualSharp", {"position": v(-45, 62.5) * mm});
            skArc(sketch, "E85.filletArc", {"start": v(-40, 62.5) * mm, "mid": v(-43.54, 61.04) * mm, "end": v(-45, 57.5) * mm});
            skPoint(sketch, "E86.visualSharp", {"position": v(45, 62.5) * mm});
            skArc(sketch, "E86.filletArc", {"start": v(45, 57.5) * mm, "mid": v(43.54, 61.04) * mm, "end": v(40, 62.5) * mm});
            skPoint(sketch, "E87.visualSharp", {"position": v(45, -62.5) * mm});
            skArc(sketch, "E87.filletArc", {"start": v(40, -62.5) * mm, "mid": v(43.54, -61.04) * mm, "end": v(45, -57.5) * mm});
            skPoint(sketch, "E88.visualSharp", {"position": v(-45, -62.5) * mm});
            skArc(sketch, "E88.filletArc", {"start": v(-45, -57.5) * mm, "mid": v(-43.54, -61.04) * mm, "end": v(-40, -62.5) * mm});
            skArc(sketch, "E89.0.startCap", {"start": v(-29, 21.9) * mm, "mid": v(-26.5, 24.4) * mm, "end": v(-24, 21.9) * mm});
            skArc(sketch, "E89.0.endCap", {"start": v(-24, 1.4) * mm, "mid": v(-26.5, -1.1) * mm, "end": v(-29, 1.4) * mm});
            skLineSegment(sketch, "E89.0.left", {"start": v(-24, 21.9) * mm, "end": v(-24, 1.4) * mm});
            skLineSegment(sketch, "E89.0.right", {"start": v(-29, 21.9) * mm, "end": v(-29, 1.4) * mm});
            skArc(sketch, "E89.1.startCap", {"start": v(24.5, 30.52) * mm, "mid": v(27, 33.02) * mm, "end": v(29.5, 30.52) * mm});
            skArc(sketch, "E89.1.endCap", {"start": v(29.5, 9.6) * mm, "mid": v(27, 7.1) * mm, "end": v(24.5, 9.6) * mm});
            skLineSegment(sketch, "E89.1.left", {"start": v(29.5, 30.52) * mm, "end": v(29.5, 9.6) * mm});
            skLineSegment(sketch, "E89.1.right", {"start": v(24.5, 30.52) * mm, "end": v(24.5, 9.6) * mm});
            skArc(sketch, "E89.2.startCap", {"start": v(24.5, -9.05) * mm, "mid": v(27, -6.55) * mm, "end": v(29.5, -9.05) * mm});
            skArc(sketch, "E89.2.endCap", {"start": v(29.5, -23.05) * mm, "mid": v(27, -25.55) * mm, "end": v(24.5, -23.05) * mm});
            skLineSegment(sketch, "E89.2.left", {"start": v(29.5, -9.05) * mm, "end": v(29.5, -23.05) * mm});
            skLineSegment(sketch, "E89.2.right", {"start": v(24.5, -9.05) * mm, "end": v(24.5, -23.05) * mm});
            skArc(sketch, "E89.3.startCap", {"start": v(-29, -10.7) * mm, "mid": v(-26.5, -8.2) * mm, "end": v(-24, -10.7) * mm});
            skArc(sketch, "E89.3.endCap", {"start": v(-24, -31.2) * mm, "mid": v(-26.5, -33.7) * mm, "end": v(-29, -31.2) * mm});
            skLineSegment(sketch, "E89.3.left", {"start": v(-24, -10.7) * mm, "end": v(-24, -31.2) * mm});
            skLineSegment(sketch, "E89.3.right", {"start": v(-29, -10.7) * mm, "end": v(-29, -31.2) * mm});
            skSolve(sketch);
        }
        {
            var Q0;
            Q0=qSketchRegion(id+"F26",true);
            extrude(context, id + "F27", {"entities" : qUnion([Q0]), "depth" : 4 * mm});
        }
        {
            var Q0;
            Q0=makeQuery(id+"F27.opExtrude","CAP_FACE",FACE,{"disambiguationData":[OSD([sQuery(id+"F26.wireOp",EDGE,"E71"),sQuery(id+"F26.wireOp",EDGE,"E72.0.1.0"),sQuery(id+"F26.wireOp",EDGE,"E73.bottom"),sQuery(id+"F26.wireOp",EDGE,"E73.top"),sQuery(id+"F26.wireOp",EDGE,"E73.left"),sQuery(id+"F26.wireOp",EDGE,"E73.right"),sQuery(id+"F26.wireOp",EDGE,"E79.0.startCap"),sQuery(id+"F26.wireOp",EDGE,"E79.0.endCap"),sQuery(id+"F26.wireOp",EDGE,"E79.0.left"),sQuery(id+"F26.wireOp",EDGE,"E79.0.right"),sQuery(id+"F26.wireOp",EDGE,"E80"),sQuery(id+"F26.wireOp",EDGE,"E81"),sQuery(id+"F26.wireOp",EDGE,"E82"),sQuery(id+"F26.wireOp",EDGE,"E83"),sQuery(id+"F26.wireOp",EDGE,"E84.0.1.0"),sQuery(id+"F26.wireOp",EDGE,"E84.0.1.1"),sQuery(id+"F26.wireOp",EDGE,"E85.filletArc"),sQuery(id+"F26.wireOp",EDGE,"E86.filletArc"),sQuery(id+"F26.wireOp",EDGE,"E87.filletArc"),sQuery(id+"F26.wireOp",EDGE,"E88.filletArc"),sQuery(id+"F26.wireOp",EDGE,"E89.0.startCap"),sQuery(id+"F26.wireOp",EDGE,"E89.0.endCap"),sQuery(id+"F26.wireOp",EDGE,"E89.0.left"),sQuery(id+"F26.wireOp",EDGE,"E89.0.right"),sQuery(id+"F26.wireOp",EDGE,"E89.1.startCap"),sQuery(id+"F26.wireOp",EDGE,"E89.1.endCap"),sQuery(id+"F26.wireOp",EDGE,"E89.1.left"),sQuery(id+"F26.wireOp",EDGE,"E89.1.right"),sQuery(id+"F26.wireOp",EDGE,"E89.2.startCap"),sQuery(id+"F26.wireOp",EDGE,"E89.2.endCap"),sQuery(id+"F26.wireOp",EDGE,"E89.2.left"),sQuery(id+"F26.wireOp",EDGE,"E89.2.right"),sQuery(id+"F26.wireOp",EDGE,"E89.3.startCap"),sQuery(id+"F26.wireOp",EDGE,"E89.3.endCap"),sQuery(id+"F26.wireOp",EDGE,"E89.3.left"),sQuery(id+"F26.wireOp",EDGE,"E89.3.right")])],"isStart":false});
            var sketch = newSketch(context, id + "F28", { "sketchPlane" : qUnion([Q0])});
            skText(sketch, "E90", { "text": "OPENBUILDS", "fontName": "OpenSans-Bold.ttf"});
            skText(sketch, "E91", { "text": "MAKERSL.COM", "fontName": "OpenSans-BoldItalic.ttf"});
            const initialGuessF28  = {"E90": [-0.0375, -0.0475, 1, 0, 0.00839], "E91": [-0.0325, 0.04958, 1, 0, 0.00679]};
            skSetInitialGuess(sketch, initialGuessF28);
            skSolve(sketch);
        }
        {
            var Q0;
            Q0=qSketchRegion(id+"F28",true);
            extrude(context, id + "F29", {"entities" : qUnion([Q0]), "operationType" : NewBodyOperationType.REMOVE, "oppositeDirection" : true, "depth" : 2 * mm});
        }
        {
            var Q0;
            {var subQ0=sQuery(id+"F26.wireOp",EDGE,"E79.0.startCap");var subQ1=sQuery(id+"F26.wireOp",EDGE,"E79.0.right");var subQ2=sQuery(id+"F26.wireOp",EDGE,"E72.0.1.0");var subQ3=sQuery(id+"F26.wireOp",EDGE,"E89.3.right");var subQ4=sQuery(id+"F26.wireOp",EDGE,"E89.3.left");var subQ5=sQuery(id+"F26.wireOp",EDGE,"E89.3.endCap");var subQ6=sQuery(id+"F26.wireOp",EDGE,"E79.0.endCap");var subQ7=sQuery(id+"F26.wireOp",EDGE,"E89.3.startCap");var subQ8=sQuery(id+"F26.wireOp",EDGE,"E89.2.right");var subQ9=sQuery(id+"F26.wireOp",EDGE,"E89.2.left");var subQ10=sQuery(id+"F26.wireOp",EDGE,"E89.2.endCap");var subQ11=sQuery(id+"F26.wireOp",EDGE,"E89.1.startCap");var subQ12=sQuery(id+"F26.wireOp",EDGE,"E73.top");var subQ13=sQuery(id+"F26.wireOp",EDGE,"E79.0.left");var subQ14=sQuery(id+"F26.wireOp",EDGE,"E87.filletArc");var subQ15=sQuery(id+"F26.wireOp",EDGE,"E88.filletArc");var subQ16=sQuery(id+"F26.wireOp",EDGE,"E89.1.left");var subQ17=sQuery(id+"F26.wireOp",EDGE,"E82");var subQ18=sQuery(id+"F26.wireOp",EDGE,"E73.bottom");var subQ19=sQuery(id+"F26.wireOp",EDGE,"E73.right");var subQ20=sQuery(id+"F26.wireOp",EDGE,"E89.2.startCap");var subQ21=sQuery(id+"F26.wireOp",EDGE,"E73.left");var subQ22=sQuery(id+"F26.wireOp",EDGE,"E86.filletArc");var subQ23=sQuery(id+"F26.wireOp",EDGE,"E89.0.left");var subQ24=sQuery(id+"F26.wireOp",EDGE,"E71");var subQ25=sQuery(id+"F26.wireOp",EDGE,"E89.0.endCap");var subQ26=sQuery(id+"F26.wireOp",EDGE,"E84.0.1.0");var subQ27=sQuery(id+"F26.wireOp",EDGE,"E85.filletArc");var subQ28=sQuery(id+"F26.wireOp",EDGE,"E84.0.1.1");var subQ29=sQuery(id+"F26.wireOp",EDGE,"E89.0.startCap");var subQ30=sQuery(id+"F26.wireOp",EDGE,"E89.1.right");var subQ31=sQuery(id+"F26.wireOp",EDGE,"E83");var subQ32=sQuery(id+"F26.wireOp",EDGE,"E89.0.right");var subQ33=sQuery(id+"F26.wireOp",EDGE,"E89.1.endCap");var subQ34=sQuery(id+"F26.wireOp",EDGE,"E81");var subQ35=sQuery(id+"F26.wireOp",EDGE,"E80");Q0=makeQuery(id+"F29.boolean.opBoolean","SPLIT",FACE,{"disambiguationData":[TD([makeQuery(id+"F27.opExtrude","SWEPT_FACE",FACE,{"disambiguationData":[OSD([subQ24])]})])],"derivedFrom":makeQuery(id+"F27.opExtrude","CAP_FACE",FACE,{"disambiguationData":[OSD([subQ24,subQ2,subQ18,subQ12,subQ21,subQ19,subQ0,subQ6,subQ13,subQ1,subQ35,subQ34,subQ17,subQ31,subQ26,subQ28,subQ27,subQ22,subQ14,subQ15,subQ29,subQ25,subQ23,subQ32,subQ11,subQ33,subQ16,subQ30,subQ20,subQ10,subQ9,subQ8,subQ7,subQ5,subQ4,subQ3])],"isStart":false})});}
            var sketch = newSketch(context, id + "F30", { "sketchPlane" : qUnion([Q0])});
            skLineSegment(sketch, "E92.bottom", {"start": v(12, -12) * mm, "end": v(-12, -12) * mm, "construction": true});
            skLineSegment(sketch, "E92.top", {"start": v(12, 12) * mm, "end": v(-12, 12) * mm, "construction": true});
            skLineSegment(sketch, "E92.left", {"start": v(12, -12) * mm, "end": v(12, 12) * mm, "construction": true});
            skLineSegment(sketch, "E92.right", {"start": v(-12, -12) * mm, "end": v(-12, 12) * mm, "construction": true});
            skPoint(sketch, "E92.middle", {"position": v(0, 0) * mm});
            skCircle(sketch, "E93", {"center": v(-12, 12) * mm, "radius": 1.1 * mm});
            skCircle(sketch, "E94.0.1.0", {"center": v(-12, -12) * mm, "radius": 1.1 * mm});
            skCircle(sketch, "E94.1.0.0", {"center": v(12, 12) * mm, "radius": 1.1 * mm});
            skCircle(sketch, "E94.1.1.0", {"center": v(12, -12) * mm, "radius": 1.1 * mm});
            skLineSegment(sketch, "E94.direction1", {"start": v(-12, 12) * mm, "end": v(12, 12) * mm, "construction": true});
            skLineSegment(sketch, "E94.direction2", {"start": v(-12, 12) * mm, "end": v(-12, -12) * mm, "construction": true});
            skCircle(sketch, "E95", {"center": v(0, 0) * mm, "radius": 14.25 * mm});
            skSolve(sketch);
        }
        {
            var Q0;
            Q0=qSketchRegion(id+"F30",true);
            extrude(context, id + "F31", {"entities" : qUnion([Q0]), "operationType" : NewBodyOperationType.REMOVE, "oppositeDirection" : true, "depth" : 25 * mm});
        }
    });
